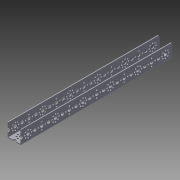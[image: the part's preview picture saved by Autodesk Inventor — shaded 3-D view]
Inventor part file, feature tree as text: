
AUTODESK INVENTOR PART (.ipt)
format: ipt  version: 2014 SP2 (Build 180246200, 246)  size: 683,520 bytes
history: native  units: in
note: dims shown in document units (in); Inventor stores cm internally (conversion verified against a paired STEP export)
features: other x1, extrude x1, imported_body x1, sketch x1
ambient origin geometry x8: Origin, YZ Plane, XZ Plane, XY Plane, X Axis, Y Axis, Z Axis, Center Point
bodies: Solid1 (feature_tree)
feature tree (4):
  other  "416mm Channel.sat1"
  extrude  "Extrusion3"  [1 undecoded]
  imported_body  "Base1"
  sketch  "Sketch3"  dims[d5=3.937in d6=0.0in]
note: 1 required parameter value undecoded (feature->parameter linkage not recoverable at this tier; creation-order binding heuristic only, values carry confidence <= 0.55)
